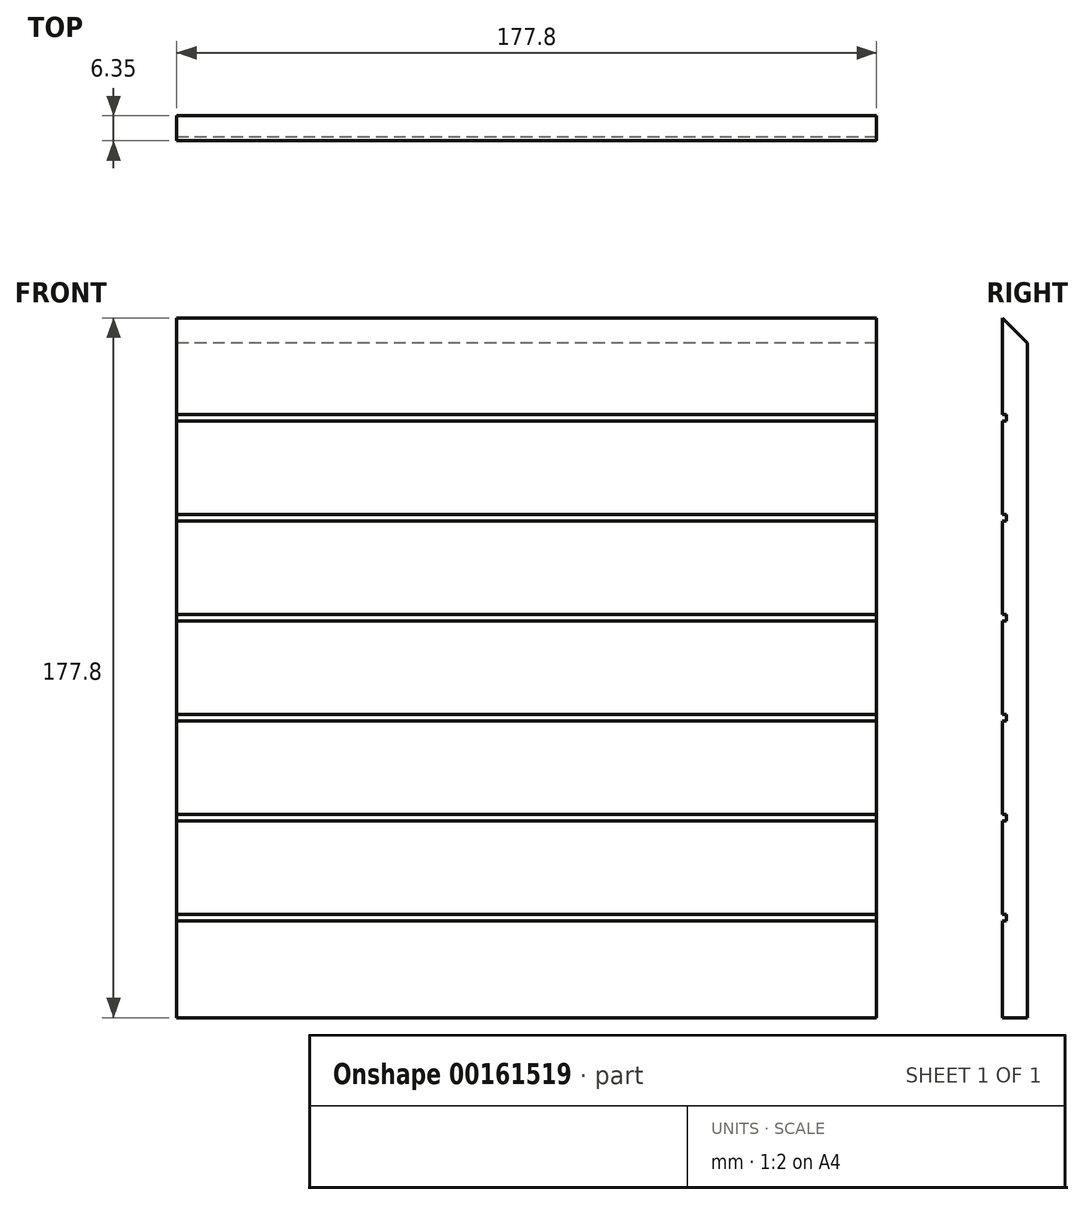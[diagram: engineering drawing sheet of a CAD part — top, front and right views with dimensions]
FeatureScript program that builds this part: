
annotation { "Feature Type Name" : "Feature", "Feature Type Description" : "" }
export const myFeature = defineFeature(function(context is Context, id is Id, definition is map)
    precondition{}
    {
        {
            var Q0;
            Q0=qCreatedBy(makeId("Front.planeOp"),FACE);
            var sketch = newSketch(context, id + "F0", { "sketchPlane" : qUnion([Q0])});
            skLineSegment(sketch, "E0.bottom", {"start": v(0, 0) * mm, "end": v(177.8, 0) * mm});
            skLineSegment(sketch, "E0.top", {"start": v(0, -177.8) * mm, "end": v(177.8, -177.8) * mm});
            skLineSegment(sketch, "E0.left", {"start": v(0, 0) * mm, "end": v(0, -177.8) * mm});
            skLineSegment(sketch, "E0.right", {"start": v(177.8, 0) * mm, "end": v(177.8, -177.8) * mm});
            skSolve(sketch);
        }
        {
            var Q0;
            Q0 = qSketchRegion(id + "F0", true);
            extrude(context, id + "F1", {"entities" : qUnion([Q0]), "depth" : 6.35 * mm});
        }
        {
            var Q0;
            Q0=makeQuery(id+"F1.opExtrude","SWEPT_FACE",FACE,{"disambiguationData":[OSD([sQuery(id+"F0.wireOp",EDGE,"E0.left")])]});
            var sketch = newSketch(context, id + "F2", { "sketchPlane" : qUnion([Q0])});
            skLineSegment(sketch, "E1", {"start": v(6.35, 0) * mm, "end": v(0, -6.35) * mm});
            skSolve(sketch);
        }
        {
            var Q0;
            Q0 = qSketchRegion(id + "F2", true);
            var Q1;
            {var subQ0=sQuery(id+"F2.wireOp",EDGE,"E1");Q1=makeQuery(id+"F2.imprint","IMPRINT",FACE,{"disambiguationData":[TD([[makeQuery(id+"F2.imprint","IMPRINT",EDGE,{"derivedFrom":subQ0}),-1.0]])]});}
            extrude(context, id + "F3", {"entities" : qUnion([Q0, Q1]), "operationType" : NewBodyOperationType.REMOVE, "endBound" : BoundingType.THROUGH_ALL, "oppositeDirection" : true, "depth" : 25.4 * mm});
        }
        {
            var Q0;
            Q0=makeQuery(id+"F1.opExtrude","CAP_FACE",FACE,{"disambiguationData":[OSD([sQuery(id+"F0.wireOp",EDGE,"E0.bottom"),sQuery(id+"F0.wireOp",EDGE,"E0.top"),sQuery(id+"F0.wireOp",EDGE,"E0.left"),sQuery(id+"F0.wireOp",EDGE,"E0.right")])],"isStart":false});
            var sketch = newSketch(context, id + "F4", { "sketchPlane" : qUnion([Q0])});
            skLineSegment(sketch, "E2.bottom", {"start": v(0, -24.6) * mm, "end": v(177.8, -24.6) * mm});
            skLineSegment(sketch, "E2.top", {"start": v(0, -26.2) * mm, "end": v(177.8, -26.2) * mm});
            skLineSegment(sketch, "E2.left", {"start": v(0, -24.6) * mm, "end": v(0, -26.2) * mm});
            skLineSegment(sketch, "E2.right", {"start": v(177.8, -24.6) * mm, "end": v(177.8, -26.2) * mm});
            skLineSegment(sketch, "E3.1.0.0", {"start": v(0, -51.6) * mm, "end": v(177.8, -51.6) * mm});
            skLineSegment(sketch, "E3.1.0.1", {"start": v(0, -50) * mm, "end": v(177.8, -50) * mm});
            skLineSegment(sketch, "E3.2.0.0", {"start": v(0, -77) * mm, "end": v(177.8, -77) * mm});
            skLineSegment(sketch, "E3.2.0.1", {"start": v(0, -75.4) * mm, "end": v(177.8, -75.4) * mm});
            skLineSegment(sketch, "E3.3.0.0", {"start": v(0, -102.4) * mm, "end": v(177.8, -102.4) * mm});
            skLineSegment(sketch, "E3.3.0.1", {"start": v(0, -100.8) * mm, "end": v(177.8, -100.8) * mm});
            skLineSegment(sketch, "E3.4.0.0", {"start": v(0, -127.8) * mm, "end": v(177.8, -127.8) * mm});
            skLineSegment(sketch, "E3.4.0.1", {"start": v(0, -126.2) * mm, "end": v(177.8, -126.2) * mm});
            skLineSegment(sketch, "E3.5.0.0", {"start": v(0, -153.2) * mm, "end": v(177.8, -153.2) * mm});
            skLineSegment(sketch, "E3.5.0.1", {"start": v(0, -151.6) * mm, "end": v(177.8, -151.6) * mm});
            skLineSegment(sketch, "E3.direction1", {"start": v(0, -26.2) * mm, "end": v(0, -51.6) * mm, "construction": true});
            skSolve(sketch);
        }
        {
            var Q0;
            Q0 = qSketchRegion(id + "F4", true);
            var Q1;
            {var subQ0=sQuery(id+"F4.wireOp",EDGE,"E3.1.0.0");Q1=makeQuery(id+"F4.imprint","IMPRINT",FACE,{"disambiguationData":[TD([[makeQuery(id+"F4.imprint","IMPRINT",EDGE,{"derivedFrom":subQ0}),1.0]])]});}
            var Q2;
            {var subQ0=sQuery(id+"F4.wireOp",EDGE,"E3.2.0.0");Q2=makeQuery(id+"F4.imprint","IMPRINT",FACE,{"disambiguationData":[TD([[makeQuery(id+"F4.imprint","IMPRINT",EDGE,{"derivedFrom":subQ0}),1.0]])]});}
            var Q3;
            {var subQ0=sQuery(id+"F4.wireOp",EDGE,"E3.3.0.0");Q3=makeQuery(id+"F4.imprint","IMPRINT",FACE,{"disambiguationData":[TD([[makeQuery(id+"F4.imprint","IMPRINT",EDGE,{"derivedFrom":subQ0}),1.0]])]});}
            var Q4;
            {var subQ0=sQuery(id+"F4.wireOp",EDGE,"E3.4.0.0");Q4=makeQuery(id+"F4.imprint","IMPRINT",FACE,{"disambiguationData":[TD([[makeQuery(id+"F4.imprint","IMPRINT",EDGE,{"derivedFrom":subQ0}),1.0]])]});}
            var Q5;
            {var subQ0=sQuery(id+"F4.wireOp",EDGE,"E3.5.0.0");Q5=makeQuery(id+"F4.imprint","IMPRINT",FACE,{"disambiguationData":[TD([[makeQuery(id+"F4.imprint","IMPRINT",EDGE,{"derivedFrom":subQ0}),1.0]])]});}
            extrude(context, id + "F5", {"entities" : qUnion([Q0, Q1, Q2, Q3, Q4, Q5]), "operationType" : NewBodyOperationType.REMOVE, "oppositeDirection" : true, "depth" : 1 * mm});
        }
    });
